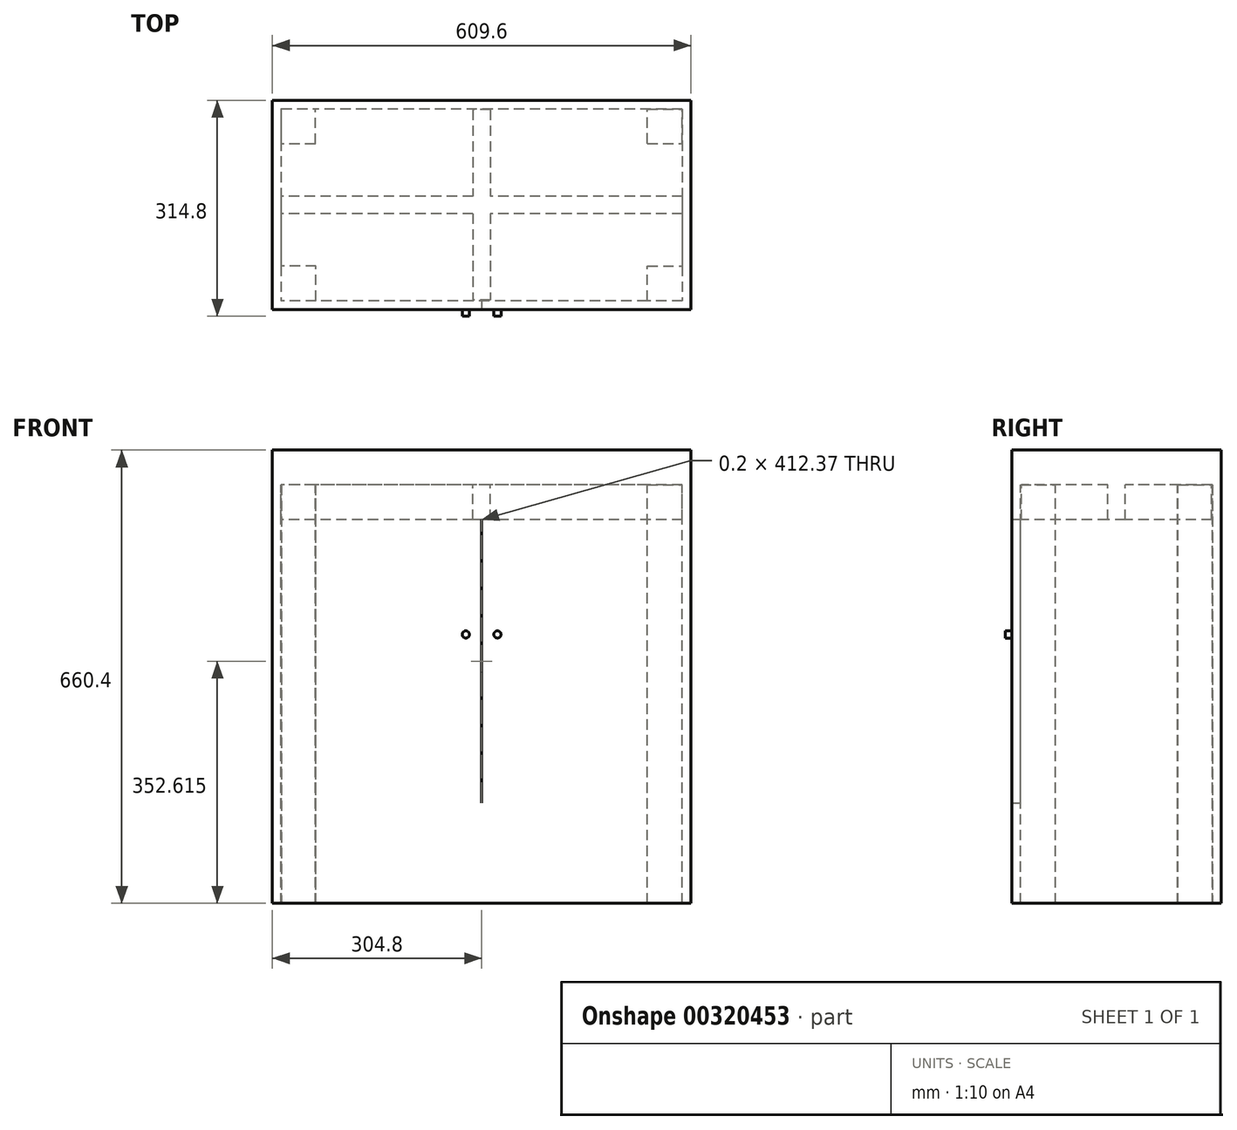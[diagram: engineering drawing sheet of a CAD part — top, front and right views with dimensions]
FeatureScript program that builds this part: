
annotation { "Feature Type Name" : "Feature", "Feature Type Description" : "" }
export const myFeature = defineFeature(function(context is Context, id is Id, definition is map)
    precondition{}
    {
        {
            var Q0;
            Q0=qCreatedBy(makeId("Top.planeOp"),FACE);
            var sketch = newSketch(context, id + "F0", { "sketchPlane" : qUnion([Q0])});
            skLineSegment(sketch, "E0.bottom", {"start": v(304.8, -152.4) * mm, "end": v(-304.8, -152.4) * mm});
            skLineSegment(sketch, "E0.top", {"start": v(304.8, 152.4) * mm, "end": v(-304.8, 152.4) * mm});
            skLineSegment(sketch, "E0.left", {"start": v(304.8, -152.4) * mm, "end": v(304.8, 152.4) * mm});
            skLineSegment(sketch, "E0.right", {"start": v(-304.8, -152.4) * mm, "end": v(-304.8, 152.4) * mm});
            skPoint(sketch, "E0.middle", {"position": v(0, 0) * mm});
            skSolve(sketch);
        }
        {
            var Q0;
            Q0=makeQuery(id+"F0.imprint","IMPRINT",FACE,{"disambiguationData":[TD([[makeQuery(id+"F0.imprint","IMPRINT",EDGE,{"derivedFrom":sQuery(id+"F0.wireOp",EDGE,"E0.bottom")}),-1.0]])]});
            extrude(context, id + "F1", {"entities" : qUnion([Q0]), "depth" : 50.8 * mm});
        }
        {
            var Q0;
            Q0=makeQuery(id+"F1.opExtrude","CAP_FACE",FACE,{"disambiguationData":[OSD([sQuery(id+"F0.wireOp",EDGE,"E0.bottom"),sQuery(id+"F0.wireOp",EDGE,"E0.top"),sQuery(id+"F0.wireOp",EDGE,"E0.left"),sQuery(id+"F0.wireOp",EDGE,"E0.right")])],"isStart":true});
            var sketch = newSketch(context, id + "F2", { "sketchPlane" : qUnion([Q0])});
            skLineSegment(sketch, "E1.bottom", {"start": v(292.1, -139.7) * mm, "end": v(-292.1, -139.7) * mm});
            skLineSegment(sketch, "E1.top", {"start": v(292.1, 139.7) * mm, "end": v(-292.1, 139.7) * mm});
            skLineSegment(sketch, "E1.left", {"start": v(292.1, -139.7) * mm, "end": v(292.1, 139.7) * mm});
            skLineSegment(sketch, "E1.right", {"start": v(-292.1, -139.7) * mm, "end": v(-292.1, 139.7) * mm});
            skPoint(sketch, "E1.middle", {"position": v(0, 0) * mm});
            skSolve(sketch);
        }
        {
            var Q0;
            Q0=makeQuery(id+"F2.imprint","IMPRINT",FACE,{"disambiguationData":[TD([[makeQuery(id+"F2.imprint","IMPRINT",EDGE,{"derivedFrom":sQuery(id+"F2.wireOp",EDGE,"E1.bottom")}),1.0]])]});
            extrude(context, id + "F3", {"entities" : qUnion([Q0]), "operationType" : NewBodyOperationType.ADD, "depth" : 50.8 * mm});
        }
        {
            var Q0;
            Q0=makeQuery(id+"F1.opExtrude","CAP_FACE",FACE,{"disambiguationData":[OSD([sQuery(id+"F0.wireOp",EDGE,"E0.bottom"),sQuery(id+"F0.wireOp",EDGE,"E0.top"),sQuery(id+"F0.wireOp",EDGE,"E0.left"),sQuery(id+"F0.wireOp",EDGE,"E0.right")])],"isStart":true});
            var sketch = newSketch(context, id + "F4", { "sketchPlane" : qUnion([Q0])});
            skLineSegment(sketch, "E2.bottom", {"start": v(292.1, -12.7) * mm, "end": v(-292.1, -12.7) * mm});
            skLineSegment(sketch, "E2.top", {"start": v(292.1, 12.7) * mm, "end": v(-292.1, 12.7) * mm});
            skLineSegment(sketch, "E2.left", {"start": v(292.1, -12.7) * mm, "end": v(292.1, 12.7) * mm});
            skLineSegment(sketch, "E2.right", {"start": v(-292.1, -12.7) * mm, "end": v(-292.1, 12.7) * mm});
            skPoint(sketch, "E2.middle", {"position": v(0, 0) * mm});
            skSolve(sketch);
        }
        {
            var Q0;
            {var subQ0=sQuery(id+"F4.wireOp",EDGE,"E2.top");Q0=makeQuery(id+"F4.imprint","IMPRINT",FACE,{"disambiguationData":[TD([[makeQuery(id+"F4.imprint","IMPRINT",EDGE,{"derivedFrom":subQ0}),-1.0]])]});}
            var sketch = newSketch(context, id + "F5", { "sketchPlane" : qUnion([Q0])});
            skLineSegment(sketch, "E3.bottom", {"start": v(12.7, -138.55) * mm, "end": v(-12.7, -138.55) * mm});
            skLineSegment(sketch, "E3.top", {"start": v(12.7, 138.55) * mm, "end": v(-12.7, 138.55) * mm});
            skLineSegment(sketch, "E3.left", {"start": v(12.7, -138.55) * mm, "end": v(12.7, 138.55) * mm});
            skLineSegment(sketch, "E3.right", {"start": v(-12.7, -138.55) * mm, "end": v(-12.7, 138.55) * mm});
            skPoint(sketch, "E3.middle", {"position": v(0, 0) * mm});
            skSolve(sketch);
        }
        {
            var Q0;
            {var subQ0=sQuery(id+"F5.wireOp",EDGE,"E3.bottom");Q0=makeQuery(id+"F5.imprint","IMPRINT",FACE,{"disambiguationData":[TD([[makeQuery(id+"F5.imprint","IMPRINT",EDGE,{"derivedFrom":subQ0}),-1.0]])]});}
            var Q1;
            Q1=makeQuery(id+"F4.imprint","IMPRINT",FACE,{"disambiguationData":[TD([[makeQuery(id+"F4.imprint","IMPRINT",EDGE,{"derivedFrom":sQuery(id+"F4.wireOp",EDGE,"E2.bottom")}),-1.0]])]});
            var Q2;
            {var subQ0=sQuery(id+"F5.wireOp",EDGE,"E3.top");Q2=makeQuery(id+"F5.imprint","IMPRINT",FACE,{"disambiguationData":[TD([[makeQuery(id+"F5.imprint","IMPRINT",EDGE,{"derivedFrom":subQ0}),1.0]])]});}
            extrude(context, id + "F6", {"entities" : qUnion([Q0, Q1, Q2]), "operationType" : NewBodyOperationType.ADD, "depth" : 50.8 * mm});
        }
        {
            var Q0;
            Q0=makeQuery(id+"F6.boolean.opBoolean","SPLIT",FACE,{"disambiguationData":[TD([makeQuery(id+"F3.opExtrude","SWEPT_FACE",FACE,{"disambiguationData":[OSD([sQuery(id+"F2.wireOp",EDGE,"E1.top")])]})])],"derivedFrom":makeQuery(id+"F1.opExtrude","CAP_FACE",FACE,{"disambiguationData":[OSD([sQuery(id+"F0.wireOp",EDGE,"E0.bottom"),sQuery(id+"F0.wireOp",EDGE,"E0.top"),sQuery(id+"F0.wireOp",EDGE,"E0.left"),sQuery(id+"F0.wireOp",EDGE,"E0.right")])],"isStart":true})});
            var sketch = newSketch(context, id + "F7", { "sketchPlane" : qUnion([Q0])});
            skLineSegment(sketch, "E4", {"start": v(0, -243.47) * mm, "end": v(0, 270.97) * mm, "construction": true});
            skLineSegment(sketch, "E5", {"start": v(-380.06, 0) * mm, "end": v(355.74, 0) * mm, "construction": true});
            skLineSegment(sketch, "E6", {"start": v(241.3, 139.7) * mm, "end": v(241.3, 88.9) * mm});
            skLineSegment(sketch, "E7", {"start": v(241.3, 88.9) * mm, "end": v(292.1, 88.9) * mm});
            skPoint(sketch, "E7.endSnap0", {"position": v(292.1, 76.2) * mm});
            skLineSegment(sketch, "E8.MirrorCS", {"start": v(241.3, -139.7) * mm, "end": v(241.3, -88.9) * mm});
            skLineSegment(sketch, "E9.MirrorCS", {"start": v(241.3, -88.9) * mm, "end": v(292.1, -88.9) * mm});
            skLineSegment(sketch, "E10.MirrorCS", {"start": v(0, 243.47) * mm, "end": v(0, -270.97) * mm, "construction": true});
            skLineSegment(sketch, "E11.MirrorCS", {"start": v(-241.3, -88.9) * mm, "end": v(-292.1, -88.9) * mm});
            skLineSegment(sketch, "E12.MirrorCS", {"start": v(-241.3, -139.7) * mm, "end": v(-241.3, -88.9) * mm});
            skLineSegment(sketch, "E13.MirrorCS", {"start": v(-241.3, 139.7) * mm, "end": v(-241.3, 88.9) * mm});
            skLineSegment(sketch, "E14.MirrorCS", {"start": v(-241.3, 88.9) * mm, "end": v(-292.1, 88.9) * mm});
            skSolve(sketch);
        }
        {
            var Q0;
            {var subQ0=sQuery(id+"F7.wireOp",EDGE,"E7");Q0=makeQuery(id+"F7.imprint","IMPRINT",FACE,{"disambiguationData":[TD([[makeQuery(id+"F7.imprint","IMPRINT",EDGE,{"derivedFrom":subQ0}),1.0]])]});}
            var sketch = newSketch(context, id + "F8", { "sketchPlane" : qUnion([Q0])});
            skLineSegment(sketch, "E15.bottom", {"start": v(241.06, -89.27) * mm, "end": v(291.75, -89.27) * mm});
            skLineSegment(sketch, "E15.top", {"start": v(241.06, -139.55) * mm, "end": v(291.75, -139.55) * mm});
            skLineSegment(sketch, "E15.left", {"start": v(241.06, -89.27) * mm, "end": v(241.06, -139.55) * mm});
            skLineSegment(sketch, "E15.right", {"start": v(291.75, -89.27) * mm, "end": v(291.75, -139.55) * mm});
            skLineSegment(sketch, "E16.bottom", {"start": v(-242.11, -88.83) * mm, "end": v(-291.67, -88.83) * mm});
            skLineSegment(sketch, "E16.top", {"start": v(-242.11, -140.1) * mm, "end": v(-291.67, -140.1) * mm});
            skLineSegment(sketch, "E16.left", {"start": v(-242.11, -88.83) * mm, "end": v(-242.11, -140.1) * mm});
            skLineSegment(sketch, "E16.right", {"start": v(-291.67, -88.83) * mm, "end": v(-291.67, -140.1) * mm});
            skSolve(sketch);
        }
        {
            var Q0;
            Q0=makeQuery(id+"F8.imprint","IMPRINT",FACE,{"disambiguationData":[TD([[makeQuery(id+"F8.imprint","IMPRINT",EDGE,{"derivedFrom":sQuery(id+"F8.wireOp",EDGE,"E16.bottom")}),1.0]])]});
            var Q1;
            {var subQ0=sQuery(id+"F7.wireOp",EDGE,"E13.MirrorCS");Q1=makeQuery(id+"F7.imprint","IMPRINT",FACE,{"disambiguationData":[TD([[makeQuery(id+"F7.imprint","IMPRINT",EDGE,{"derivedFrom":subQ0}),-1.0]])]});}
            var Q2;
            Q2=makeQuery(id+"F8.imprint","IMPRINT",FACE,{"disambiguationData":[TD([[makeQuery(id+"F8.imprint","IMPRINT",EDGE,{"derivedFrom":sQuery(id+"F8.wireOp",EDGE,"E15.bottom")}),-1.0]])]});
            var Q3;
            {var subQ0=sQuery(id+"F7.wireOp",EDGE,"E7");Q3=makeQuery(id+"F7.imprint","IMPRINT",FACE,{"disambiguationData":[TD([[makeQuery(id+"F7.imprint","IMPRINT",EDGE,{"derivedFrom":subQ0}),1.0]])]});}
            extrude(context, id + "F9", {"entities" : qUnion([Q0, Q1, Q2, Q3]), "operationType" : NewBodyOperationType.ADD, "depth" : 609.6 * mm});
        }
        {
            var Q0;
            Q0=makeQuery(id+"F6.boolean.opBoolean","MERGE",FACE,{"derivedFrom":[makeQuery(id+"F3.opExtrude","CAP_FACE",FACE,{"disambiguationData":[OSD([sQuery(id+"F0.wireOp",EDGE,"E0.bottom"),sQuery(id+"F0.wireOp",EDGE,"E0.top"),sQuery(id+"F0.wireOp",EDGE,"E0.left"),sQuery(id+"F0.wireOp",EDGE,"E0.right"),sQuery(id+"F2.wireOp",EDGE,"E1.bottom"),sQuery(id+"F2.wireOp",EDGE,"E1.top"),sQuery(id+"F2.wireOp",EDGE,"E1.left"),sQuery(id+"F2.wireOp",EDGE,"E1.right")])],"isStart":false}),makeQuery(id+"F6.opExtrude","CAP_FACE",FACE,{"disambiguationData":[OSD([sQuery(id+"F4.wireOp",EDGE,"E2.bottom"),sQuery(id+"F4.wireOp",EDGE,"E2.top"),sQuery(id+"F4.wireOp",EDGE,"E2.left"),sQuery(id+"F4.wireOp",EDGE,"E2.right")])],"isStart":false}),makeQuery(id+"F6.opExtrude","CAP_FACE",FACE,{"disambiguationData":[OSD([sQuery(id+"F5.wireOp",EDGE,"E3.bottom"),sQuery(id+"F5.wireOp",EDGE,"E3.top"),sQuery(id+"F5.wireOp",EDGE,"E3.left"),sQuery(id+"F5.wireOp",EDGE,"E3.right")])],"isStart":false})]});
            var sketch = newSketch(context, id + "F10", { "sketchPlane" : qUnion([Q0])});
            skLineSegment(sketch, "E17", {"start": v(292.1, -139.7) * mm, "end": v(304.8, -152.4) * mm});
            skLineSegment(sketch, "E18", {"start": v(-292.1, -139.7) * mm, "end": v(-304.8, -152.4) * mm});
            skSolve(sketch);
        }
        {
            var Q0;
            Q0=makeQuery(id+"F10.imprint","IMPRINT",FACE,{"disambiguationData":[TD([[makeQuery(id+"F10.imprint","IMPRINT",EDGE,{"derivedFrom":sQuery(id+"F10.wireOp",EDGE,"E17")}),-1.0]])]});
            extrude(context, id + "F11", {"entities" : qUnion([Q0]), "operationType" : NewBodyOperationType.ADD, "depth" : 558.7 * mm});
        }
        {
            var Q0;
            Q0=makeQuery(id+"F6.boolean.opBoolean","MERGE",FACE,{"derivedFrom":[makeQuery(id+"F3.opExtrude","CAP_FACE",FACE,{"disambiguationData":[OSD([sQuery(id+"F0.wireOp",EDGE,"E0.bottom"),sQuery(id+"F0.wireOp",EDGE,"E0.top"),sQuery(id+"F0.wireOp",EDGE,"E0.left"),sQuery(id+"F0.wireOp",EDGE,"E0.right"),sQuery(id+"F2.wireOp",EDGE,"E1.bottom"),sQuery(id+"F2.wireOp",EDGE,"E1.top"),sQuery(id+"F2.wireOp",EDGE,"E1.left"),sQuery(id+"F2.wireOp",EDGE,"E1.right")])],"isStart":false}),makeQuery(id+"F6.opExtrude","CAP_FACE",FACE,{"disambiguationData":[OSD([sQuery(id+"F4.wireOp",EDGE,"E2.bottom"),sQuery(id+"F4.wireOp",EDGE,"E2.top"),sQuery(id+"F4.wireOp",EDGE,"E2.left"),sQuery(id+"F4.wireOp",EDGE,"E2.right")])],"isStart":false}),makeQuery(id+"F6.opExtrude","CAP_FACE",FACE,{"disambiguationData":[OSD([sQuery(id+"F5.wireOp",EDGE,"E3.bottom"),sQuery(id+"F5.wireOp",EDGE,"E3.top"),sQuery(id+"F5.wireOp",EDGE,"E3.left"),sQuery(id+"F5.wireOp",EDGE,"E3.right")])],"isStart":false})]});
            var sketch = newSketch(context, id + "F12", { "sketchPlane" : qUnion([Q0])});
            skLineSegment(sketch, "E19", {"start": v(292.1, -12.7) * mm, "end": v(292.1, 12.7) * mm});
            skLineSegment(sketch, "E20", {"start": v(292.1, 139.7) * mm, "end": v(292.1, 152.4) * mm});
            skLineSegment(sketch, "E21", {"start": v(-292.1, 139.7) * mm, "end": v(-292.1, 152.4) * mm});
            skLineSegment(sketch, "E22", {"start": v(-292.1, -12.7) * mm, "end": v(-292.1, 12.7) * mm});
            skSolve(sketch);
        }
        {
            var Q0;
            Q0=makeQuery(id+"F12.imprint","IMPRINT",FACE,{"disambiguationData":[TD([[makeQuery(id+"F12.imprint","IMPRINT",EDGE,{"derivedFrom":sQuery(id+"F12.wireOp",EDGE,"E19")}),-1.0]])]});
            var Q1;
            {var subQ13=sQuery(id+"F12.wireOp",EDGE,"E21");Q1=makeQuery(id+"F12.imprint","IMPRINT",FACE,{"disambiguationData":[TD([[makeQuery(id+"F12.imprint","IMPRINT",EDGE,{"derivedFrom":subQ13}),1.0]])]});}
            extrude(context, id + "F13", {"entities" : qUnion([Q0, Q1]), "operationType" : NewBodyOperationType.ADD, "depth" : 558.7 * mm});
        }
        {
            var Q0;
            {var subQ1=sQuery(id+"F2.wireOp",EDGE,"E1.left");var subQ2=makeQuery(id+"F3.opExtrude","SWEPT_FACE",FACE,{"disambiguationData":[OSD([subQ1])]});var subQ3=sQuery(id+"F2.wireOp",EDGE,"E1.bottom");var subQ9=makeQuery(id+"F3.opExtrude","SWEPT_FACE",FACE,{"disambiguationData":[OSD([subQ3])]});Q0=makeQuery(id+"F11.boolean.opBoolean","MERGE",FACE,{"derivedFrom":[makeQuery(id+"F9.boolean.opBoolean","SPLIT",FACE,{"disambiguationData":[TD([subQ2])],"derivedFrom":subQ9}),makeQuery(id+"F11.opExtrude","SWEPT_FACE",FACE,{"disambiguationData":[OSD([subQ3]),TDD([makeQuery(id+"F10.imprint","IMPRINT",EDGE,{"derivedFrom":makeQuery(id+"F9.boolean.opBoolean","SPLIT",EDGE,{"disambiguationData":[TD([subQ2])],"derivedFrom":makeQuery(id+"F3.opExtrude","CAP_EDGE",EDGE,{"disambiguationData":[OSD([subQ3])],"isStart":false})})})])]})]});}
            var sketch = newSketch(context, id + "F14", { "sketchPlane" : qUnion([Q0])});
            skLineSegment(sketch, "E23", {"start": v(-242.11, -471.96) * mm, "end": v(238.35, -471.96) * mm});
            skLineSegment(sketch, "E24", {"start": v(-239.83, -500.2) * mm, "end": v(238.35, -500.2) * mm});
            skSolve(sketch);
        }
        {
            var Q0;
            Q0=sQuery(id+"F14.wireOp",EDGE,"E24");
            var Q1;
            Q1=sQuery(id+"F14.wireOp",EDGE,"E23");
            extrude(context, id + "F15", {"bodyType" : ToolBodyType.SURFACE, "surfaceEntities" : qUnion([Q0, Q1]), "depth" : 279.2 * mm});
        }
        {
            var Q0;
            Q0=makeQuery(id+"F13.boolean.opBoolean","SPLIT",FACE,{"derivedFrom":makeQuery(id+"F13.opExtrude","SWEPT_FACE",FACE,{"disambiguationData":[OSD([sQuery(id+"F2.wireOp",EDGE,"E1.right"),sQuery(id+"F12.wireOp",EDGE,"E21"),sQuery(id+"F12.wireOp",EDGE,"E22")])]})});
            var sketch = newSketch(context, id + "F16", { "sketchPlane" : qUnion([Q0])});
            skLineSegment(sketch, "E25", {"start": v(-139.7, -485.65) * mm, "end": v(-152.4, -485.65) * mm});
            skSolve(sketch);
        }
        {
            var Q0;
            {var subQ0=sQuery(id+"F16.wireOp",EDGE,"E25");Q0=makeQuery(id+"F16.imprint","IMPRINT",FACE,{"disambiguationData":[TD([[makeQuery(id+"F16.imprint","IMPRINT",EDGE,{"derivedFrom":subQ0}),1.0]])]});}
            extrude(context, id + "F17", {"entities" : qUnion([Q0]), "operationType" : NewBodyOperationType.ADD, "depth" : 583.42 * mm});
        }
        {
            var Q0;
            Q0=makeQuery(id+"F17.opExtrude","SWEPT_FACE",FACE,{"disambiguationData":[OSD([sQuery(id+"F16.wireOp",EDGE,"E25")])]});
            extrude(context, id + "F18", {"entities" : qUnion([Q0]), "operationType" : NewBodyOperationType.ADD, "depth" : 22.48 * mm});
        }
        {
            var Q0;
            Q0=makeQuery(id+"F13.boolean.opBoolean","SPLIT",FACE,{"derivedFrom":makeQuery(id+"F13.opExtrude","SWEPT_FACE",FACE,{"disambiguationData":[OSD([sQuery(id+"F2.wireOp",EDGE,"E1.right"),sQuery(id+"F12.wireOp",EDGE,"E21"),sQuery(id+"F12.wireOp",EDGE,"E22")])]})});
            extrude(context, id + "F19", {"entities" : qUnion([Q0]), "operationType" : NewBodyOperationType.ADD, "depth" : 292 * mm});
        }
        {
            var Q0;
            {var subQ0=sQuery(id+"F12.wireOp",EDGE,"E21");var subQ1=sQuery(id+"F0.wireOp",EDGE,"E0.bottom");var subQ2=makeQuery(id+"F3.opExtrude","CAP_EDGE",EDGE,{"disambiguationData":[OSD([subQ1])],"isStart":false});Q0=makeQuery(id+"F19.boolean.opBoolean","MERGE",FACE,{"derivedFrom":[makeQuery(id+"F18.boolean.opBoolean","MERGE",FACE,{"derivedFrom":[makeQuery(id+"F17.boolean.opBoolean","MERGE",FACE,{"derivedFrom":[makeQuery(id+"F13.boolean.opBoolean","MERGE",FACE,{"derivedFrom":[makeQuery(id+"F3.boolean.opBoolean","MERGE",FACE,{"derivedFrom":[makeQuery(id+"F1.opExtrude","SWEPT_FACE",FACE,{"disambiguationData":[OSD([subQ1])]}),makeQuery(id+"F3.opExtrude","SWEPT_FACE",FACE,{"disambiguationData":[OSD([subQ1])]})]}),makeQuery(id+"F13.opExtrude","SWEPT_FACE",FACE,{"disambiguationData":[OSD([subQ1]),TDD([makeQuery(id+"F12.imprint","IMPRINT",EDGE,{"disambiguationData":[TD([[makeQuery(id+"F12.imprint","INTERSECT",VERTEX,{"derivedFrom":[subQ2,makeQuery(id+"F3.opExtrude","CAP_EDGE",EDGE,{"disambiguationData":[OSD([sQuery(id+"F0.wireOp",EDGE,"E0.left")])],"isStart":false})]}),-1.0]])],"derivedFrom":subQ2})])]}),makeQuery(id+"F13.opExtrude","SWEPT_FACE",FACE,{"disambiguationData":[OSD([subQ1]),TDD([makeQuery(id+"F12.imprint","IMPRINT",EDGE,{"disambiguationData":[TD([[makeQuery(id+"F12.imprint","INTERSECT",VERTEX,{"derivedFrom":[subQ2,makeQuery(id+"F3.opExtrude","CAP_EDGE",EDGE,{"disambiguationData":[OSD([sQuery(id+"F0.wireOp",EDGE,"E0.right")])],"isStart":false})]}),1.0]])],"derivedFrom":subQ2})])]})]}),makeQuery(id+"F17.opExtrude","SWEPT_FACE",FACE,{"disambiguationData":[OSD([subQ1,subQ0])]})]}),makeQuery(id+"F18.opExtrude","SWEPT_FACE",FACE,{"disambiguationData":[OSD([subQ1,subQ0,sQuery(id+"F16.wireOp",EDGE,"E25")])]})]}),makeQuery(id+"F19.opExtrude","SWEPT_FACE",FACE,{"disambiguationData":[OSD([subQ1,subQ0])]})]});}
            var sketch = newSketch(context, id + "F20", { "sketchPlane" : qUnion([Q0])});
            skLineSegment(sketch, "E26.bottom", {"start": v(-0.1, -50.8) * mm, "end": v(-292.1, -50.8) * mm});
            skLineSegment(sketch, "E26.top", {"start": v(-0.1, -463.17) * mm, "end": v(-292.1, -463.17) * mm});
            skLineSegment(sketch, "E26.left", {"start": v(-0.1, -50.8) * mm, "end": v(-0.1, -463.17) * mm});
            skLineSegment(sketch, "E26.right", {"start": v(-292.1, -50.8) * mm, "end": v(-292.1, -463.17) * mm});
            skSolve(sketch);
        }
        {
            var Q0;
            Q0=makeQuery(id+"F13.boolean.opBoolean","SPLIT",FACE,{"derivedFrom":makeQuery(id+"F13.opExtrude","SWEPT_FACE",FACE,{"disambiguationData":[OSD([sQuery(id+"F2.wireOp",EDGE,"E1.left"),sQuery(id+"F12.wireOp",EDGE,"E19"),sQuery(id+"F12.wireOp",EDGE,"E20")])]})});
            extrude(context, id + "F21", {"entities" : qUnion([Q0]), "operationType" : NewBodyOperationType.ADD, "depth" : 292 * mm});
        }
        {
            var Q0;
            {var subQ0=sQuery(id+"F12.wireOp",EDGE,"E20");var subQ1=sQuery(id+"F0.wireOp",EDGE,"E0.bottom");var subQ2=sQuery(id+"F12.wireOp",EDGE,"E21");var subQ3=makeQuery(id+"F3.opExtrude","CAP_EDGE",EDGE,{"disambiguationData":[OSD([subQ1])],"isStart":false});Q0=makeQuery(id+"F21.boolean.opBoolean","MERGE",FACE,{"derivedFrom":[makeQuery(id+"F19.boolean.opBoolean","MERGE",FACE,{"derivedFrom":[makeQuery(id+"F18.boolean.opBoolean","MERGE",FACE,{"derivedFrom":[makeQuery(id+"F17.boolean.opBoolean","MERGE",FACE,{"derivedFrom":[makeQuery(id+"F13.boolean.opBoolean","MERGE",FACE,{"derivedFrom":[makeQuery(id+"F3.boolean.opBoolean","MERGE",FACE,{"derivedFrom":[makeQuery(id+"F1.opExtrude","SWEPT_FACE",FACE,{"disambiguationData":[OSD([subQ1])]}),makeQuery(id+"F3.opExtrude","SWEPT_FACE",FACE,{"disambiguationData":[OSD([subQ1])]})]}),makeQuery(id+"F13.opExtrude","SWEPT_FACE",FACE,{"disambiguationData":[OSD([subQ1]),TDD([makeQuery(id+"F12.imprint","IMPRINT",EDGE,{"disambiguationData":[TD([[makeQuery(id+"F12.imprint","INTERSECT",VERTEX,{"derivedFrom":[subQ3,makeQuery(id+"F3.opExtrude","CAP_EDGE",EDGE,{"disambiguationData":[OSD([sQuery(id+"F0.wireOp",EDGE,"E0.left")])],"isStart":false})]}),-1.0]])],"derivedFrom":subQ3})])]}),makeQuery(id+"F13.opExtrude","SWEPT_FACE",FACE,{"disambiguationData":[OSD([subQ1]),TDD([makeQuery(id+"F12.imprint","IMPRINT",EDGE,{"disambiguationData":[TD([[makeQuery(id+"F12.imprint","INTERSECT",VERTEX,{"derivedFrom":[subQ3,makeQuery(id+"F3.opExtrude","CAP_EDGE",EDGE,{"disambiguationData":[OSD([sQuery(id+"F0.wireOp",EDGE,"E0.right")])],"isStart":false})]}),1.0]])],"derivedFrom":subQ3})])]})]}),makeQuery(id+"F17.opExtrude","SWEPT_FACE",FACE,{"disambiguationData":[OSD([subQ1,subQ2])]})]}),makeQuery(id+"F18.opExtrude","SWEPT_FACE",FACE,{"disambiguationData":[OSD([subQ1,subQ2,sQuery(id+"F16.wireOp",EDGE,"E25")])]})]}),makeQuery(id+"F19.opExtrude","SWEPT_FACE",FACE,{"disambiguationData":[OSD([subQ1,subQ2])]})]}),makeQuery(id+"F21.opExtrude","SWEPT_FACE",FACE,{"disambiguationData":[OSD([subQ1,subQ0])]})]});}
            var sketch = newSketch(context, id + "F22", { "sketchPlane" : qUnion([Q0])});
            skLineSegment(sketch, "E27.bottom", {"start": v(0.1, -50.8) * mm, "end": v(292.1, -50.8) * mm});
            skLineSegment(sketch, "E27.top", {"start": v(0.1, -463.2) * mm, "end": v(292.1, -463.2) * mm});
            skLineSegment(sketch, "E27.left", {"start": v(0.1, -50.8) * mm, "end": v(0.1, -463.2) * mm});
            skLineSegment(sketch, "E27.right", {"start": v(292.1, -50.8) * mm, "end": v(292.1, -463.2) * mm});
            skSolve(sketch);
        }
        {
            var Q0;
            {var subQ4=sQuery(id+"F22.wireOp",EDGE,"E27.bottom");Q0=makeQuery(id+"F22.imprint","IMPRINT",FACE,{"disambiguationData":[TD([[makeQuery(id+"F22.imprint","IMPRINT",EDGE,{"derivedFrom":subQ4}),-1.0]])]});}
            var sketch = newSketch(context, id + "F23", { "sketchPlane" : qUnion([Q0])});
            skCircle(sketch, "E28", {"center": v(22.94, -217.82) * mm, "radius": 5.25 * mm});
            skCircle(sketch, "E29.MirrorC", {"center": v(-23.14, -217.82) * mm, "radius": 5.25 * mm});
            skSolve(sketch);
        }
        {
            var Q0;
            Q0 = qSketchRegion(id + "F23", true);
            extrude(context, id + "F24", {"entities" : qUnion([Q0]), "operationType" : NewBodyOperationType.ADD, "depth" : 10 * mm});
        }
    });
